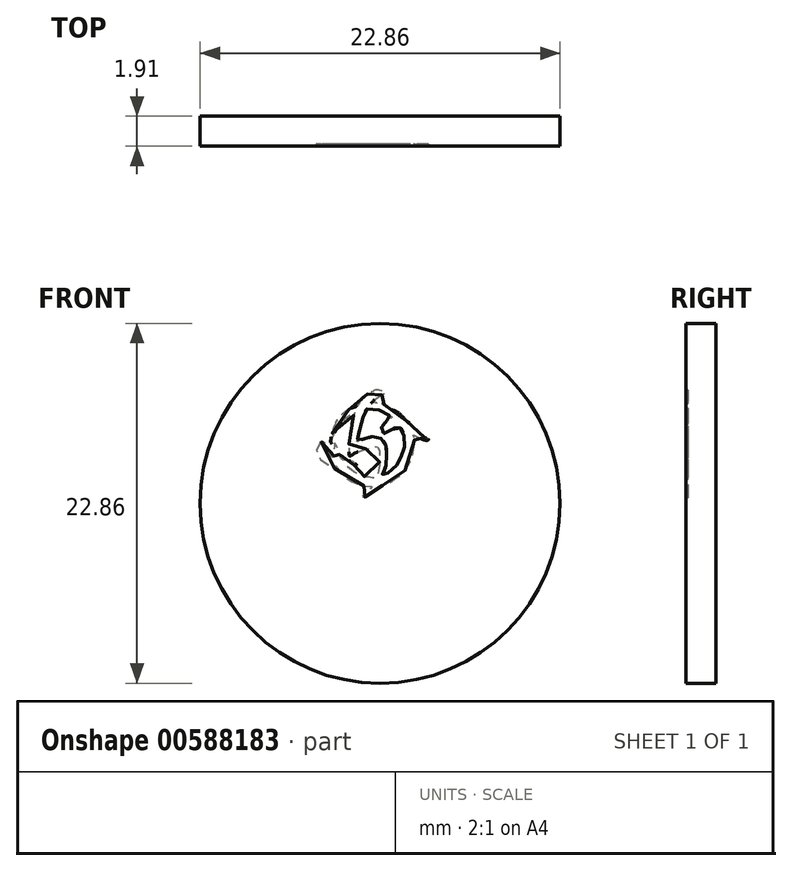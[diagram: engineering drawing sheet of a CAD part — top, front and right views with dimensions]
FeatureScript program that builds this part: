
annotation { "Feature Type Name" : "Feature", "Feature Type Description" : "" }
export const myFeature = defineFeature(function(context is Context, id is Id, definition is map)
    precondition{}
    {
        {
            var Q0;
            Q0=qCreatedBy(makeId("Front.planeOp"),FACE);
            var sketch = newSketch(context, id + "F0", { "sketchPlane" : qUnion([Q0])});
            skCircle(sketch, "E0", {"center": v(0, 0) * mm, "radius": 11.43 * mm});
            skSolve(sketch);
        }
        {
            var Q0;
            Q0 = qSketchRegion(id + "F0", true);
            extrude(context, id + "F1", {"entities" : qUnion([Q0]), "depth" : 1.9 * mm, "offsetDistance" : 25.4 * mm});
        }
        {
            var Q0;
            Q0=makeQuery(id+"F1.opExtrude","CAP_FACE",FACE,{"disambiguationData":[OSD([sQuery(id+"F0.wireOp",EDGE,"E0")])],"isStart":false});
            var sketch = newSketch(context, id + "F2", { "sketchPlane" : qUnion([Q0])});
            skFitSpline(sketch, "E1", {"points": [v(-3.76, 3.94) * mm, v(-4.07, 3.54) * mm, v(-4.01, 3.3) * mm, v(-3.87, 2.9) * mm, v(-3.54, 2.6) * mm, v(-3.17, 2.36) * mm, v(-2.87, 2.24) * mm, v(-2.83, 2.36) * mm, v(-2.61, 2) * mm, v(-2.25, 1.72) * mm, v(-1.82, 1.37) * mm, v(-1.25, 1.17) * mm, v(-0.82, 1.06) * mm, v(-0.5, 1.08) * mm, v(-0.6, 0.96) * mm, v(-0.69, 0.81) * mm, v(-0.84, 0.63) * mm, v(-0.97, 0.52) * mm, v(-1.1, 0.44) * mm, v(-1.12, 0.34) * mm, v(-0.97, 0.39) * mm, v(-0.8, 0.45) * mm, v(-0.7, 0.5) * mm, v(-0.54, 0.63) * mm, v(-0.42, 0.73) * mm, v(-0.34, 0.85) * mm, v(-0.29, 0.93) * mm, v(-0.23, 1) * mm, v(-0.2, 1.09) * mm, v(0.01, 1.12) * mm, v(0.22, 1.17) * mm, v(0.44, 1.24) * mm, v(0.65, 1.34) * mm, v(0.86, 1.5) * mm, v(1.02, 1.59) * mm, v(1.22, 1.7) * mm, v(1.38, 1.85) * mm, v(1.53, 2.02) * mm, v(1.68, 2.26) * mm, v(1.82, 2.51) * mm, v(1.93, 2.68) * mm, v(2.05, 3.03) * mm, v(2.14, 3.36) * mm, v(2.2, 3.72) * mm, v(2.17, 4.04) * mm, v(2.12, 4.33) * mm, v(2.27, 4.25) * mm, v(2.46, 4.15) * mm, v(2.71, 4.04) * mm, v(2.92, 4) * mm, v(3.06, 4.02) * mm, v(3.09, 4.07) * mm, v(2.87, 4.16) * mm, v(2.74, 4.26) * mm, v(2.64, 4.38) * mm, v(2.47, 4.5) * mm, v(2.34, 4.61) * mm, v(2.24, 4.72) * mm, v(2.05, 4.87) * mm, v(1.95, 4.96) * mm, v(1.86, 5.12) * mm, v(1.69, 5.23) * mm, v(1.54, 5.39) * mm, v(1.35, 5.57) * mm, v(1.24, 5.69) * mm, v(1.04, 5.82) * mm, v(0.87, 5.9) * mm, v(0.63, 6.03) * mm, v(0.44, 6.2) * mm, v(0.13, 6.3) * mm, v(-0.06, 6.3) * mm, v(-0.36, 6.4) * mm, v(-0.54, 6.38) * mm, v(-0.44, 6.49) * mm, v(-0.36, 6.6) * mm, v(-0.24, 6.67) * mm, v(-0.02, 6.8) * mm, v(0.12, 6.9) * mm, v(0.31, 7) * mm, v(0.37, 7.09) * mm, v(0.1, 7.15) * mm, v(-0.1, 7.2) * mm, v(-0.26, 7.2) * mm, v(-0.42, 7.14) * mm, v(-0.54, 7.08) * mm, v(-0.7, 7) * mm, v(-0.89, 6.88) * mm, v(-1.06, 6.74) * mm, v(-1.18, 6.61) * mm, v(-1.28, 6.47) * mm, v(-1.33, 6.36) * mm, v(-1.45, 6.2) * mm, v(-1.7, 6.08) * mm, v(-1.86, 6.01) * mm, v(-2, 5.94) * mm, v(-2.2, 5.8) * mm, v(-2.4, 5.65) * mm, v(-2.63, 5.42) * mm, v(-2.77, 5.24) * mm, v(-2.87, 5) * mm, v(-2.98, 4.75) * mm, v(-3.03, 4.5) * mm, v(-3.12, 4.27) * mm, v(-3.13, 4.03) * mm, v(-3.14, 3.86) * mm, v(-3.08, 3.82) * mm, v(-3.06, 4.04) * mm, v(-3.01, 4.2) * mm, v(-2.93, 4.39) * mm, v(-2.8, 4.64) * mm, v(-2.68, 4.82) * mm, v(-2.53, 5.05) * mm, v(-2.37, 5.3) * mm, v(-2.2, 5.41) * mm, v(-2.02, 5.54) * mm, v(-1.78, 5.71) * mm, v(-1.6, 5.8) * mm, v(-1.68, 5.61) * mm, v(-1.79, 5.35) * mm, v(-1.82, 5.23) * mm, v(-1.9, 4.88) * mm, v(-1.9, 4.72) * mm, v(-1.94, 4.42) * mm, v(-1.95, 4.18) * mm, v(-1.97, 3.9) * mm, v(-1.99, 3.56) * mm, v(-1.97, 3.29) * mm, v(-1.94, 3) * mm, v(-1.68, 3.15) * mm, v(-1.5, 3.24) * mm, v(-1.24, 3.3) * mm, v(-1, 3.42) * mm, v(-0.73, 3.49) * mm, v(-0.41, 3.58) * mm, v(-0.27, 3.62) * mm, v(-0.14, 3.57) * mm, v(-0.04, 3.32) * mm, v(-0.04, 3.09) * mm, v(-0.03, 2.9) * mm, v(-0.03, 2.69) * mm, v(-0.05, 2.5) * mm, v(-0.06, 2.2) * mm, v(-0.15, 1.87) * mm, v(-0.2, 1.68) * mm, v(-0.34, 1.62) * mm, v(-0.54, 1.62) * mm, v(-0.77, 1.67) * mm, v(-0.99, 1.7) * mm, v(-1.23, 1.74) * mm, v(-1.37, 1.84) * mm, v(-1.58, 1.97) * mm, v(-1.75, 2.06) * mm, v(-1.92, 2.2) * mm, v(-2.1, 2.38) * mm, v(-1.83, 2.4) * mm, v(-1.6, 2.44) * mm, v(-1.5, 2.45) * mm, v(-1.64, 2.57) * mm, v(-1.76, 2.65) * mm, v(-1.94, 2.7) * mm, v(-2.1, 2.72) * mm, v(-2.29, 2.76) * mm, v(-2.39, 2.76) * mm, v(-2.52, 2.96) * mm, v(-2.61, 3.2) * mm, v(-2.65, 3.39) * mm, v(-2.74, 3.62) * mm, v(-2.83, 3.75) * mm, v(-2.9, 3.82) * mm, v(-2.9, 3.56) * mm, v(-2.93, 3.44) * mm, v(-2.94, 3.24) * mm, v(-2.94, 3.09) * mm, v(-2.94, 2.9) * mm, v(-3.08, 2.97) * mm, v(-3.2, 3.07) * mm, v(-3.35, 3.22) * mm, v(-3.38, 3.35) * mm, v(-3.46, 3.58) * mm, v(-3.5, 3.8) * mm, v(-3.63, 3.92) * mm, v(-3.76, 3.94) * mm]});
            skFitSpline(sketch, "E2", {"points": [v(-0.84, 6) * mm, v(-0.48, 6) * mm, v(-0.1, 5.92) * mm, v(0.27, 5.82) * mm, v(0.48, 5.67) * mm, v(0.76, 5.45) * mm, v(0.6, 5.39) * mm, v(0.45, 5.27) * mm, v(0.26, 5.14) * mm, v(0.1, 4.96) * mm, v(0.1, 4.74) * mm, v(0.11, 4.57) * mm, v(0.1, 4.44) * mm, v(0.37, 4.46) * mm, v(0.52, 4.6) * mm, v(0.67, 4.65) * mm, v(0.85, 4.76) * mm, v(1.03, 4.78) * mm, v(1.2, 4.78) * mm, v(1.35, 4.75) * mm, v(1.45, 4.55) * mm, v(1.52, 4.37) * mm, v(1.53, 4.08) * mm, v(1.55, 3.7) * mm, v(1.55, 3.46) * mm, v(1.45, 3.22) * mm, v(1.32, 2.91) * mm, v(1.26, 2.7) * mm, v(1.1, 2.52) * mm, v(0.94, 2.29) * mm, v(0.72, 2.1) * mm, v(0.43, 1.9) * mm, v(0.2, 1.77) * mm, v(0.1, 1.75) * mm, v(0.21, 1.94) * mm, v(0.3, 2.15) * mm, v(0.37, 2.34) * mm, v(0.38, 2.6) * mm, v(0.4, 2.87) * mm, v(0.4, 3.11) * mm, v(0.4, 3.33) * mm, v(0.4, 3.53) * mm, v(0.34, 3.74) * mm, v(0.26, 3.9) * mm, v(0.1, 4.08) * mm, v(-0.1, 4.19) * mm, v(-0.26, 4.2) * mm, v(-0.49, 4.23) * mm, v(-0.63, 4.2) * mm, v(-0.85, 4.15) * mm, v(-1.05, 4.08) * mm, v(-1.28, 4) * mm, v(-1.46, 3.92) * mm, v(-1.4, 4.12) * mm, v(-1.39, 4.3) * mm, v(-1.28, 4.77) * mm, v(-1.19, 5.23) * mm, v(-1.11, 5.38) * mm, v(-1.02, 5.64) * mm, v(-0.93, 5.82) * mm, v(-0.84, 6) * mm]});
            skLineSegment(sketch, "E3", {"start": v(0.1, 0.4) * mm, "end": v(0.1, 8.03) * mm, "construction": true});
            skSolve(sketch);
        }
        {
            var Q0;
            Q0 = qSketchRegion(id + "F2", true);
            extrude(context, id + "F3", {"entities" : qUnion([Q0]), "operationType" : NewBodyOperationType.REMOVE, "oppositeDirection" : true, "depth" : 0.13 * mm, "offsetDistance" : 25.4 * mm});
        }
    });
